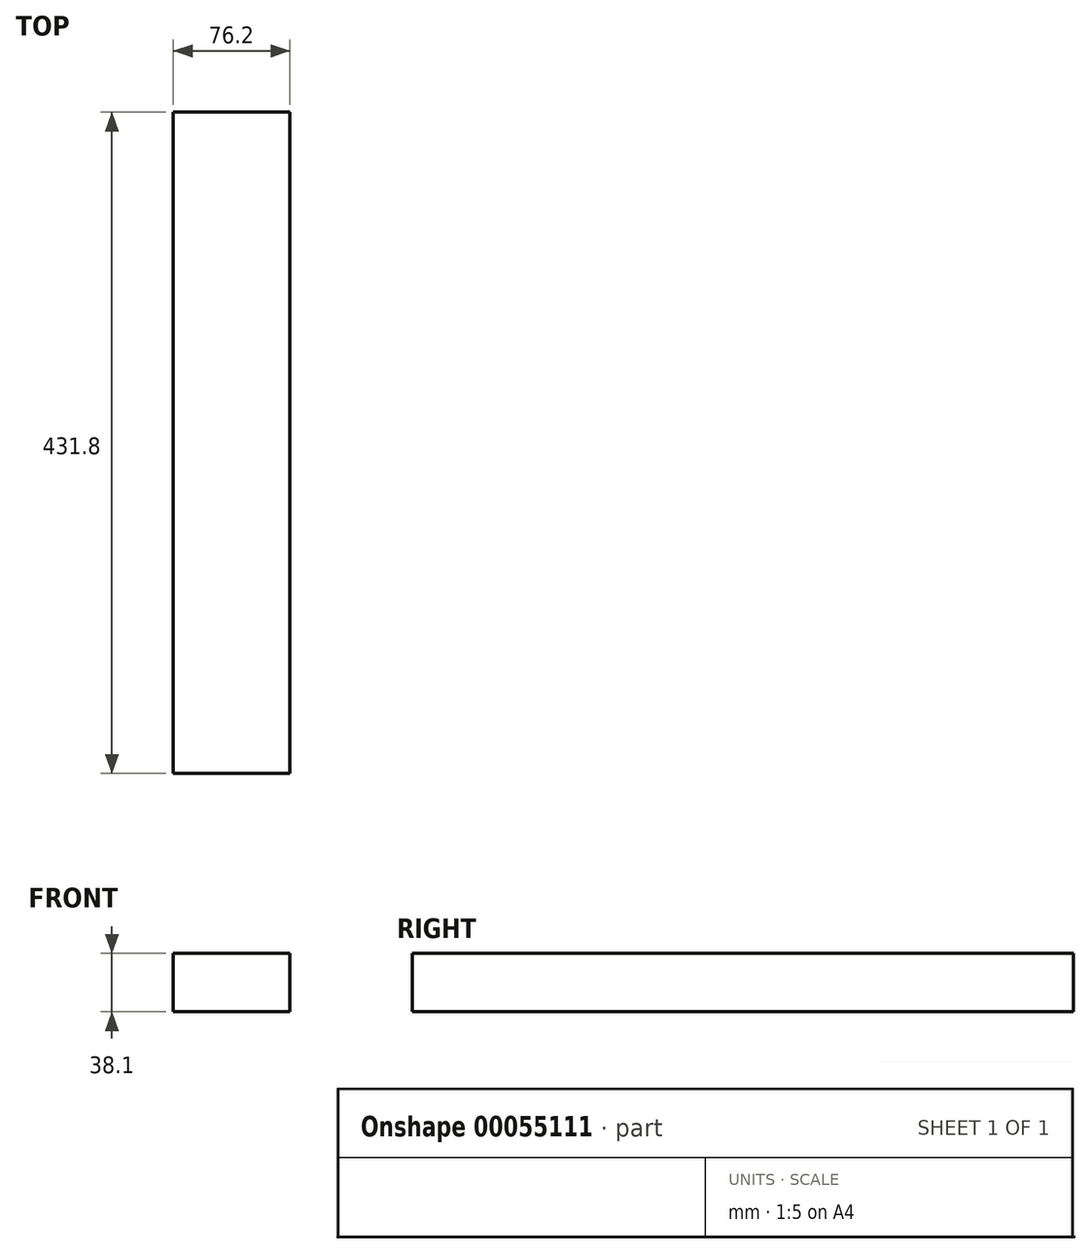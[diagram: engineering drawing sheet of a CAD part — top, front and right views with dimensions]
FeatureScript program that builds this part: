
annotation { "Feature Type Name" : "Feature", "Feature Type Description" : "" }
export const myFeature = defineFeature(function(context is Context, id is Id, definition is map)
    precondition{}
    {
        {
            var Q0;
            Q0=qCreatedBy(makeId("Front.planeOp"),FACE);
            var sketch = newSketch(context, id + "F0", { "sketchPlane" : qUnion([Q0])});
            skLineSegment(sketch, "E0.bottom", {"start": v(-38.1, -19.05) * mm, "end": v(38.1, -19.05) * mm});
            skLineSegment(sketch, "E0.top", {"start": v(-38.1, 19.05) * mm, "end": v(38.1, 19.05) * mm});
            skLineSegment(sketch, "E0.left", {"start": v(-38.1, -19.05) * mm, "end": v(-38.1, 19.05) * mm});
            skLineSegment(sketch, "E0.right", {"start": v(38.1, -19.05) * mm, "end": v(38.1, 19.05) * mm});
            skLineSegment(sketch, "E1", {"start": v(-38.1, 19.05) * mm, "end": v(0, 0) * mm, "construction": true});
            skLineSegment(sketch, "E2", {"start": v(0, 0) * mm, "end": v(38.1, -19.05) * mm, "construction": true});
            skSolve(sketch);
        }
        {
            var Q0;
            Q0 = qSketchRegion(id + "F0", true);
            extrude(context, id + "F1", {"entities" : qUnion([Q0]), "depth" : 431.8 * mm});
        }
    });
